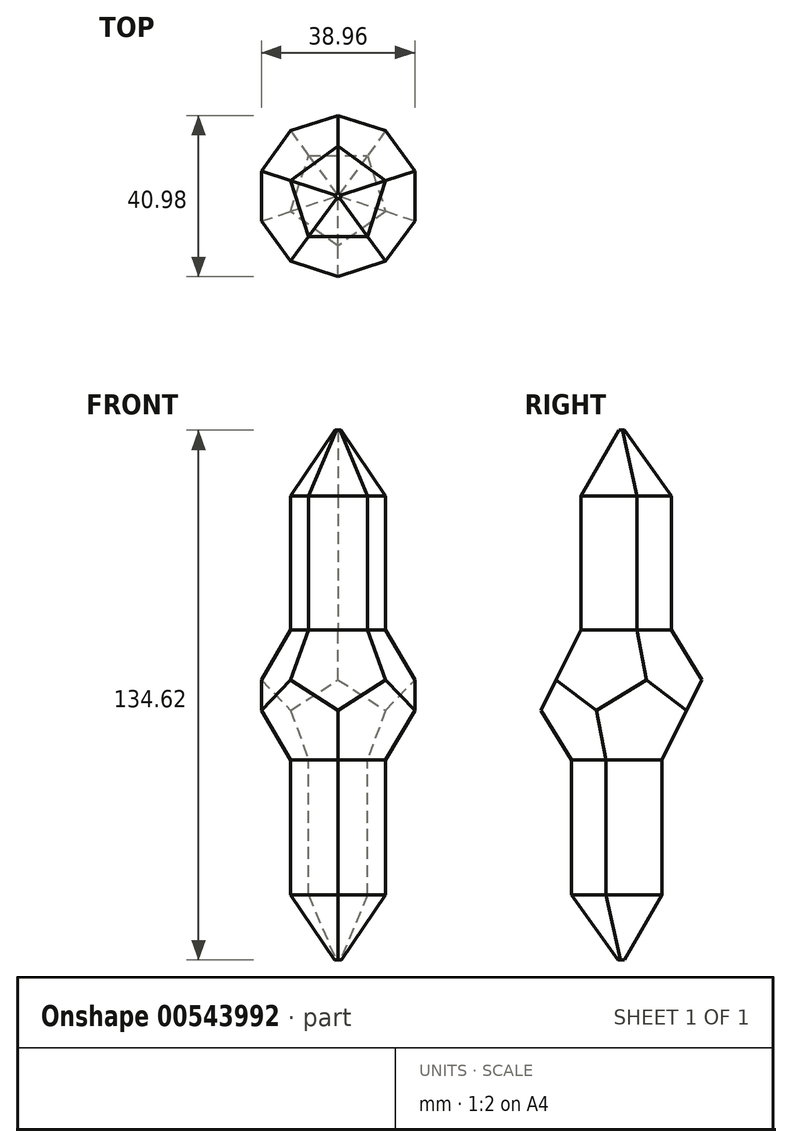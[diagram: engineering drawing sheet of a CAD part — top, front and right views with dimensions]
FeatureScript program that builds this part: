
annotation { "Feature Type Name" : "Feature", "Feature Type Description" : "" }
export const myFeature = defineFeature(function(context is Context, id is Id, definition is map)
    precondition{}
    {
        {
            var Q0;
            Q0=qCreatedBy(makeId("Top.planeOp"),FACE);
            var sketch = newSketch(context, id + "F0", { "sketchPlane" : qUnion([Q0])});
            skCircle(sketch, "E0.cCircle", {"center": v(0, 0) * mm, "radius": 12.7 * mm, "construction": true});
            skLineSegment(sketch, "E0.0", {"start": v(7.46, 10.27) * mm, "end": v(12.08, -3.92) * mm});
            skLineSegment(sketch, "E0.1", {"start": v(12.08, -3.92) * mm, "end": v(0, -12.7) * mm});
            skLineSegment(sketch, "E0.2", {"start": v(0, -12.7) * mm, "end": v(-12.08, -3.92) * mm});
            skLineSegment(sketch, "E0.3", {"start": v(-12.08, -3.92) * mm, "end": v(-7.46, 10.27) * mm});
            skLineSegment(sketch, "E0.4", {"start": v(-7.46, 10.27) * mm, "end": v(7.46, 10.27) * mm});
            skSolve(sketch);
        }
        {
            var Q0;
            Q0 = qSketchRegion(id + "F0", true);
            extrude(context, id + "F1", {"entities" : qUnion([Q0]), "depth" : 33.02 * mm, "offsetDistance" : 25.4 * mm, "hasDraft" : true, "draftAngle" : 26.57 * degree});
        }
        {
            var Q0;
            Q0=makeQuery(id+"F1.opExtrude","CAP_FACE",FACE,{"disambiguationData":[OSD([sQuery(id+"F0.wireOp",EDGE,"E0.0"),sQuery(id+"F0.wireOp",EDGE,"E0.1"),sQuery(id+"F0.wireOp",EDGE,"E0.2"),sQuery(id+"F0.wireOp",EDGE,"E0.3"),sQuery(id+"F0.wireOp",EDGE,"E0.4")])],"isStart":false});
            var sketch = newSketch(context, id + "F2", { "sketchPlane" : qUnion([Q0])});
            skCircle(sketch, "E1.cCircle", {"center": v(0, 0) * mm, "radius": 12.7 * mm, "construction": true});
            skLineSegment(sketch, "E1.0", {"start": v(7.46, 10.27) * mm, "end": v(12.08, -3.92) * mm, "construction": true});
            skLineSegment(sketch, "E1.1", {"start": v(12.08, -3.92) * mm, "end": v(0, -12.7) * mm, "construction": true});
            skLineSegment(sketch, "E1.2", {"start": v(0, -12.7) * mm, "end": v(-12.08, -3.92) * mm, "construction": true});
            skLineSegment(sketch, "E1.3", {"start": v(-12.08, -3.92) * mm, "end": v(-7.46, 10.27) * mm, "construction": true});
            skLineSegment(sketch, "E1.4", {"start": v(-7.46, 10.27) * mm, "end": v(7.46, 10.27) * mm, "construction": true});
            skLineSegment(sketch, "E2", {"start": v(-28.2, 0) * mm, "end": v(27.51, 0) * mm, "construction": true});
            skLineSegment(sketch, "E3.MirrorCS", {"start": v(12.08, 3.92) * mm, "end": v(0, 12.7) * mm});
            skLineSegment(sketch, "E4.MirrorCS", {"start": v(7.46, -10.27) * mm, "end": v(12.08, 3.92) * mm});
            skLineSegment(sketch, "E5.MirrorCS", {"start": v(-7.46, -10.27) * mm, "end": v(7.46, -10.27) * mm});
            skLineSegment(sketch, "E6.MirrorCS", {"start": v(-12.08, 3.92) * mm, "end": v(-7.46, -10.27) * mm});
            skLineSegment(sketch, "E7.MirrorCS", {"start": v(0, 12.7) * mm, "end": v(-12.08, 3.92) * mm});
            skSolve(sketch);
        }
        {
            var Q0;
            Q0 = qSketchRegion(id + "F2", true);
            extrude(context, id + "F3", {"entities" : qUnion([Q0]), "operationType" : NewBodyOperationType.INTERSECT, "oppositeDirection" : true, "depth" : 33.02 * mm, "offsetDistance" : 25.4 * mm, "hasDraft" : true, "draftAngle" : 26.57 * degree});
        }
        {
            var Q0;
            Q0=makeQuery(id+"F1.opExtrude","CAP_FACE",FACE,{"disambiguationData":[OSD([sQuery(id+"F0.wireOp",EDGE,"E0.0"),sQuery(id+"F0.wireOp",EDGE,"E0.1"),sQuery(id+"F0.wireOp",EDGE,"E0.2"),sQuery(id+"F0.wireOp",EDGE,"E0.3"),sQuery(id+"F0.wireOp",EDGE,"E0.4")])],"isStart":false});
            var sketch = newSketch(context, id + "F4", { "sketchPlane" : qUnion([Q0])});
            skLineSegment(sketch, "E8.0", {"start": v(-7.46, -10.27) * mm, "end": v(7.46, -10.27) * mm});
            skLineSegment(sketch, "E9.0", {"start": v(7.46, -10.27) * mm, "end": v(12.08, 3.92) * mm});
            skLineSegment(sketch, "E10.0", {"start": v(-12.08, 3.92) * mm, "end": v(-7.46, -10.27) * mm});
            skLineSegment(sketch, "E10.1", {"start": v(0, 12.7) * mm, "end": v(-12.08, 3.92) * mm});
            skLineSegment(sketch, "E10.2", {"start": v(12.08, 3.92) * mm, "end": v(0, 12.7) * mm});
            skSolve(sketch);
        }
        {
            var Q0;
            Q0 = qSketchRegion(id + "F4", true);
            extrude(context, id + "F5", {"entities" : qUnion([Q0]), "operationType" : NewBodyOperationType.ADD, "depth" : 50.8 * mm, "offsetDistance" : 25.4 * mm});
        }
        {
            var Q0;
            Q0=makeQuery(id+"F5.opExtrude","CAP_EDGE",EDGE,{"disambiguationData":[OSD([sQuery(id+"F4.wireOp",EDGE,"E9.0")])],"isStart":false});
            var Q1;
            Q1=makeQuery(id+"F5.opExtrude","CAP_EDGE",EDGE,{"disambiguationData":[OSD([sQuery(id+"F4.wireOp",EDGE,"E8.0")])],"isStart":false});
            var Q2;
            Q2=makeQuery(id+"F5.opExtrude","CAP_EDGE",EDGE,{"disambiguationData":[OSD([sQuery(id+"F4.wireOp",EDGE,"E10.0")])],"isStart":false});
            var Q3;
            Q3=makeQuery(id+"F5.opExtrude","CAP_EDGE",EDGE,{"disambiguationData":[OSD([sQuery(id+"F4.wireOp",EDGE,"E10.1")])],"isStart":false});
            var Q4;
            Q4=makeQuery(id+"F5.opExtrude","CAP_EDGE",EDGE,{"disambiguationData":[OSD([sQuery(id+"F4.wireOp",EDGE,"E10.2")])],"isStart":false});
            chamfer(context, id + "F6", {"entities" : qUnion([Q0, Q1, Q2, Q3, Q4]), "chamferType" : ChamferType.OFFSET_ANGLE, "width" : 9.65 * mm, "oppositeDirection" : false, "angle" : 60 * degree, "tangentPropagation" : true});
        }
        {
            var Q0;
            Q0=makeQuery(id+"F1.opExtrude","CAP_FACE",FACE,{"disambiguationData":[OSD([sQuery(id+"F0.wireOp",EDGE,"E0.0"),sQuery(id+"F0.wireOp",EDGE,"E0.1"),sQuery(id+"F0.wireOp",EDGE,"E0.2"),sQuery(id+"F0.wireOp",EDGE,"E0.3"),sQuery(id+"F0.wireOp",EDGE,"E0.4")])],"isStart":true});
            var sketch = newSketch(context, id + "F7", { "sketchPlane" : qUnion([Q0])});
            skLineSegment(sketch, "E11.0", {"start": v(-12.08, 3.92) * mm, "end": v(-7.46, -10.27) * mm});
            skLineSegment(sketch, "E12.0", {"start": v(0, 12.7) * mm, "end": v(-12.08, 3.92) * mm});
            skLineSegment(sketch, "E13.0", {"start": v(12.08, 3.92) * mm, "end": v(0, 12.7) * mm});
            skLineSegment(sketch, "E14.0", {"start": v(7.46, -10.27) * mm, "end": v(12.08, 3.92) * mm});
            skLineSegment(sketch, "E15.0", {"start": v(-7.46, -10.27) * mm, "end": v(7.46, -10.27) * mm});
            skSolve(sketch);
        }
        {
            var Q0;
            Q0 = qSketchRegion(id + "F7", true);
            extrude(context, id + "F8", {"entities" : qUnion([Q0]), "operationType" : NewBodyOperationType.ADD, "depth" : 50.8 * mm, "offsetDistance" : 25.4 * mm});
        }
        {
            var Q0;
            Q0=makeQuery(id+"F8.opExtrude","CAP_EDGE",EDGE,{"disambiguationData":[OSD([sQuery(id+"F7.wireOp",EDGE,"E11.0")])],"isStart":false});
            var Q1;
            Q1=makeQuery(id+"F8.opExtrude","CAP_EDGE",EDGE,{"disambiguationData":[OSD([sQuery(id+"F7.wireOp",EDGE,"E15.0")])],"isStart":false});
            var Q2;
            Q2=makeQuery(id+"F8.opExtrude","CAP_EDGE",EDGE,{"disambiguationData":[OSD([sQuery(id+"F7.wireOp",EDGE,"E14.0")])],"isStart":false});
            var Q3;
            Q3=makeQuery(id+"F8.opExtrude","CAP_EDGE",EDGE,{"disambiguationData":[OSD([sQuery(id+"F7.wireOp",EDGE,"E13.0")])],"isStart":false});
            var Q4;
            Q4=makeQuery(id+"F8.opExtrude","CAP_EDGE",EDGE,{"disambiguationData":[OSD([sQuery(id+"F7.wireOp",EDGE,"E12.0")])],"isStart":false});
            chamfer(context, id + "F9", {"entities" : qUnion([Q0, Q1, Q2, Q3, Q4]), "chamferType" : ChamferType.OFFSET_ANGLE, "width" : 16.5 * mm, "oppositeDirection" : true, "angle" : 30 * degree, "tangentPropagation" : true});
        }
    });
